# Revit family: BRACOUBEL_60W_3000K_MAT
name_source: partatom
category: Lighting Fixtures
units: mm (PartAtom-declared; Revit-internal decimal feet)

## family parameters
Always vertical = Yes
Cut with Voids When Loaded = No
Light Source = Yes
OmniClass Number = 23.80.70.00
OmniClass Title = Lighting
Part Type = Normal
Room Calculation Point = No
Round Connector Dimension = Use Diameter
Shared = No
Work Plane-Based = No

## types (1)
- BRACOUBEL_60W_3000K_MAT
    Alimentation Driver = AC 220-240V
    Color Filter = 16777215
    Default Elevation = 0 mm  [stored 0 ft]
    Diffuseur = Transparent
    Dimensions = 300 x 800 x 4500 mm
    Dimming Lamp Color Temperature Shift = <None>
    Driver = Driver 24V ref 708222
    Fintion = Gris anthracite (RAL 7016 sa�né)
    Light Source Symbol Size = 610 mm
    Matériau = Fonte
    Puissance nominale = 60W
    Type = Mât
    Type de lampe = LED

note: [stored X ft] marks values corroborated as IEEE doubles in the binary element streams (Revit-internal decimal feet)

## geometry (parser evidence)
native form markers: Sweep x3
no freeform markers — native parametric forms only
